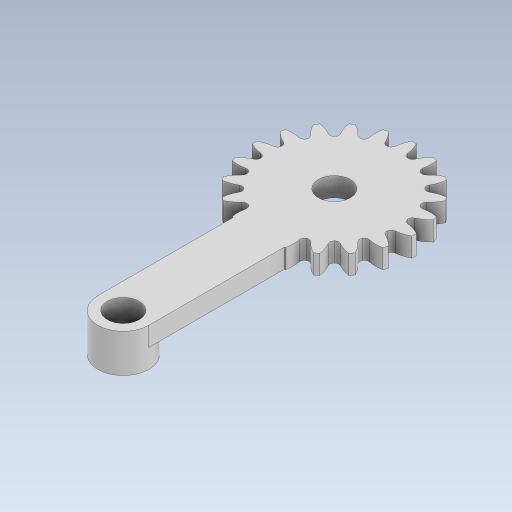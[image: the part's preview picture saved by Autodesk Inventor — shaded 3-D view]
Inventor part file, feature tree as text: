
AUTODESK INVENTOR PART (.ipt)
format: ipt  version: 2023.5 (Build 275446000, 446)  size: 527,360 bytes
history: native  units: in
note: dims shown in document units (in); Inventor stores cm internally (conversion verified against a paired STEP export)
features: extrude x4, sketch x2, fillet x1, pattern_circular x1, plane x1
ambient origin geometry x8: Origin, YZ Plane, XZ Plane, XY Plane, X Axis, Y Axis, Z Axis, Center Point
bodies: Solid1 (feature_tree)
feature tree (9):
  sketch  "Sketch1"  dims[d0=0.7874in d1=0.9843in]
  extrude  "Extrusion1"  Depth=0.9843in
  extrude  "Extrusion3"  Depth=0.1181in
  fillet  "Fillet1"  Radius=0.0276in
  pattern_circular  "Circular Pattern1"  [2 undecoded]
  plane  "Work Plane1"
  sketch  "Sketch2"  dims[d2=0.9055in d3=0.0787in d4=0.0276in d5=0.1181in d6=0.0in d9=0.1181in d10=0.0in d11=0.0276in d12=7.874in d13=360.0deg d15=0.1969in d16=0.315in d17=1.2992in d18=0.2756in d19=0.1969in d20=0.1181in d21=0.0in d22=0.1772in d23=0.0in d24=0.0197in d25=0.0344in]
  extrude  "Extrusion4"  Depth=0.1181in TaperAngle=0.0deg
  extrude  "Extrusion5"  Depth=0.0276in
note: 2 required parameter values undecoded (feature->parameter linkage not recoverable at this tier; creation-order binding heuristic only, values carry confidence <= 0.55)
